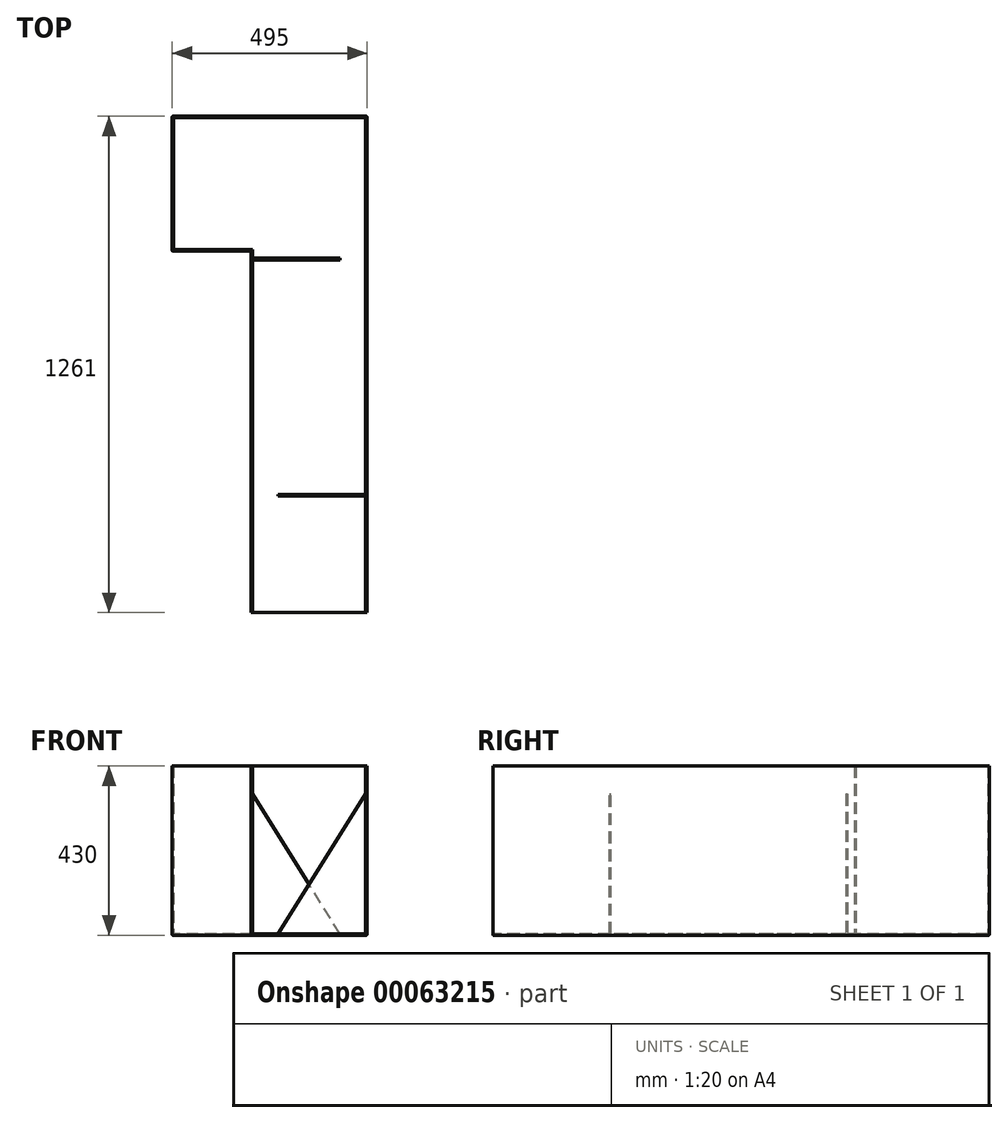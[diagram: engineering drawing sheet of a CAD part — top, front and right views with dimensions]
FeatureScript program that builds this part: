
annotation { "Feature Type Name" : "Feature", "Feature Type Description" : "" }
export const myFeature = defineFeature(function(context is Context, id is Id, definition is map)
    precondition{}
    {
        {
            var Q0;
            Q0=qCreatedBy(makeId("Top.planeOp"),FACE);
            var sketch = newSketch(context, id + "F0", { "sketchPlane" : qUnion([Q0])});
            skLineSegment(sketch, "E0", {"start": v(0, 0) * mm, "end": v(495, 0) * mm});
            skLineSegment(sketch, "E1", {"start": v(200, -343) * mm, "end": v(0, -343) * mm});
            skLineSegment(sketch, "E2", {"start": v(0, -343) * mm, "end": v(0, 0) * mm});
            skLineSegment(sketch, "E3.right", {"start": v(200, -343) * mm, "end": v(200, -1261) * mm});
            skLineSegment(sketch, "E4.left", {"start": v(495, 0) * mm, "end": v(495, -1261) * mm});
            skLineSegment(sketch, "E5.0", {"start": v(491, -4) * mm, "end": v(491, -1261) * mm});
            skLineSegment(sketch, "E5.1", {"start": v(204, -339) * mm, "end": v(204, -1261) * mm});
            skLineSegment(sketch, "E5.2", {"start": v(204, -339) * mm, "end": v(4, -339) * mm});
            skLineSegment(sketch, "E5.3", {"start": v(4, -339) * mm, "end": v(4, -4) * mm});
            skLineSegment(sketch, "E5.4", {"start": v(4, -4) * mm, "end": v(491, -4) * mm});
            skLineSegment(sketch, "E6", {"start": v(204, -1261) * mm, "end": v(200, -1261) * mm});
            skLineSegment(sketch, "E7", {"start": v(491, -1261) * mm, "end": v(495, -1261) * mm});
            skSolve(sketch);
        }
        {
            var Q0;
            Q0=makeQuery(id+"F0.imprint","IMPRINT",FACE,{"disambiguationData":[TD([[makeQuery(id+"F0.imprint","IMPRINT",EDGE,{"derivedFrom":sQuery(id+"F0.wireOp",EDGE,"E0")}),-1.0]])]});
            extrude(context, id + "F1", {"entities" : qUnion([Q0]), "depth" : 426 * mm});
        }
        {
            var Q0;
            Q0=qCreatedBy(makeId("Top.planeOp"),FACE);
            var sketch = newSketch(context, id + "F2", { "sketchPlane" : qUnion([Q0])});
            skLineSegment(sketch, "E8.0", {"start": v(200, -343) * mm, "end": v(0, -343) * mm});
            skLineSegment(sketch, "E9.0", {"start": v(0, -343) * mm, "end": v(0, 0) * mm});
            skLineSegment(sketch, "E10.0", {"start": v(0, 0) * mm, "end": v(0, 0) * mm});
            skLineSegment(sketch, "E11.0", {"start": v(0, 0) * mm, "end": v(495, 0) * mm});
            skLineSegment(sketch, "E12.0", {"start": v(200, -343) * mm, "end": v(200, -343) * mm});
            skLineSegment(sketch, "E13.0", {"start": v(495, 0) * mm, "end": v(495, 0) * mm});
            skLineSegment(sketch, "E14.0", {"start": v(495, 0) * mm, "end": v(495, -1261) * mm});
            skLineSegment(sketch, "E15", {"start": v(495, -1261) * mm, "end": v(200, -1261) * mm});
            skLineSegment(sketch, "E16", {"start": v(200, -1261) * mm, "end": v(200, -343) * mm});
            skSolve(sketch);
        }
        {
            var Q0;
            Q0=qSketchRegion(id+"F2",true);
            extrude(context, id + "F3", {"entities" : qUnion([Q0]), "operationType" : NewBodyOperationType.ADD, "oppositeDirection" : true, "depth" : 4 * mm});
        }
        {
            var Q0;
            Q0=makeQuery(id+"F3.opExtrude","CAP_EDGE",EDGE,{"disambiguationData":[OSD([sQuery(id+"F2.wireOp",EDGE,"E13.0")])],"isStart":false});
            var Q1;
            Q1=makeQuery(id+"F3.opExtrude","CAP_EDGE",EDGE,{"disambiguationData":[OSD([sQuery(id+"F2.wireOp",EDGE,"E8.0")])],"isStart":false});
            var Q2;
            Q2=makeQuery(id+"F3.opExtrude","CAP_EDGE",EDGE,{"disambiguationData":[OSD([sQuery(id+"F2.wireOp",EDGE,"E12.0")])],"isStart":false});
            var Q3;
            Q3=makeQuery(id+"F3.opExtrude","CAP_EDGE",EDGE,{"disambiguationData":[OSD([sQuery(id+"F2.wireOp",EDGE,"E9.0")])],"isStart":false});
            var Q4;
            Q4=makeQuery(id+"F3.opExtrude","CAP_EDGE",EDGE,{"disambiguationData":[OSD([sQuery(id+"F2.wireOp",EDGE,"E11.0")])],"isStart":false});
            var Q5;
            Q5=makeQuery(id+"F3.boolean.opBoolean","MERGE",EDGE,{"derivedFrom":[makeQuery(id+"F1.opExtrude","SWEPT_EDGE",EDGE,{"disambiguationData":[OSD([sQuery(id+"F0.wireOp",EDGE,"E1"),sQuery(id+"F0.wireOp",EDGE,"E3.right")])]}),makeQuery(id+"F3.opExtrude","SWEPT_EDGE",EDGE,{"disambiguationData":[OSD([sQuery(id+"F2.wireOp",EDGE,"E8.0"),sQuery(id+"F2.wireOp",EDGE,"E12.0")])]})]});
            var Q6;
            Q6=makeQuery(id+"F3.boolean.opBoolean","MERGE",EDGE,{"derivedFrom":[makeQuery(id+"F1.opExtrude","SWEPT_EDGE",EDGE,{"disambiguationData":[OSD([sQuery(id+"F0.wireOp",EDGE,"E1"),sQuery(id+"F0.wireOp",EDGE,"E2")])]}),makeQuery(id+"F3.opExtrude","SWEPT_EDGE",EDGE,{"disambiguationData":[OSD([sQuery(id+"F2.wireOp",EDGE,"E8.0"),sQuery(id+"F2.wireOp",EDGE,"E9.0")])]})]});
            var Q7;
            Q7=makeQuery(id+"F3.boolean.opBoolean","MERGE",EDGE,{"derivedFrom":[makeQuery(id+"F1.opExtrude","SWEPT_EDGE",EDGE,{"disambiguationData":[OSD([sQuery(id+"F0.wireOp",EDGE,"E0"),sQuery(id+"F0.wireOp",EDGE,"E2")])]}),makeQuery(id+"F3.opExtrude","SWEPT_EDGE",EDGE,{"disambiguationData":[OSD([sQuery(id+"F2.wireOp",EDGE,"E9.0"),sQuery(id+"F2.wireOp",EDGE,"E11.0")])]})]});
            var Q8;
            Q8=makeQuery(id+"F1.opExtrude","SWEPT_EDGE",EDGE,{"disambiguationData":[OSD([sQuery(id+"F0.wireOp",EDGE,"41269a5a-69f6-4670-b1a7-19bf830e781a"),sQuery(id+"F0.wireOp",EDGE,"E4.right")])]});
            var Q9;
            Q9=makeQuery(id+"F1.opExtrude","SWEPT_EDGE",EDGE,{"disambiguationData":[OSD([sQuery(id+"F0.wireOp",EDGE,"cc5772d9-c29a-4c81-bde5-837d5d9decb7"),sQuery(id+"F0.wireOp",EDGE,"E3.left")])]});
            var Q10;
            Q10=makeQuery(id+"F1.opExtrude","SWEPT_EDGE",EDGE,{"disambiguationData":[OSD([sQuery(id+"F0.wireOp",EDGE,"41269a5a-69f6-4670-b1a7-19bf830e781a"),sQuery(id+"F0.wireOp",EDGE,"05cfef9b-c223-4bdb-b400-77ea615546ad")])]});
            var Q11;
            Q11=makeQuery(id+"F1.opExtrude","SWEPT_EDGE",EDGE,{"disambiguationData":[OSD([sQuery(id+"F0.wireOp",EDGE,"05cfef9b-c223-4bdb-b400-77ea615546ad"),sQuery(id+"F0.wireOp",EDGE,"cc5772d9-c29a-4c81-bde5-837d5d9decb7")])]});
            var Q12;
            Q12=makeQuery(id+"F3.boolean.opBoolean","MERGE",EDGE,{"derivedFrom":[makeQuery(id+"F1.opExtrude","SWEPT_EDGE",EDGE,{"disambiguationData":[OSD([sQuery(id+"F0.wireOp",EDGE,"E0"),sQuery(id+"F0.wireOp",EDGE,"E4.left")])]}),makeQuery(id+"F3.opExtrude","SWEPT_EDGE",EDGE,{"disambiguationData":[OSD([sQuery(id+"F2.wireOp",EDGE,"E11.0"),sQuery(id+"F2.wireOp",EDGE,"E13.0")])]})]});
            var Q13;
            Q13=makeQuery(id+"F3.opExtrude","CAP_EDGE",EDGE,{"disambiguationData":[OSD([sQuery(id+"F2.wireOp",EDGE,"E16")])],"isStart":false});
            var Q14;
            Q14=makeQuery(id+"F3.opExtrude","CAP_EDGE",EDGE,{"disambiguationData":[OSD([sQuery(id+"F2.wireOp",EDGE,"E14.0")])],"isStart":false});
            fillet(context, id + "F4", {"entities" : qUnion([Q0, Q1, Q2, Q3, Q4, Q5, Q6, Q7, Q8, Q9, Q10, Q11, Q12, Q13, Q14]), "radius" : 2 * mm, "tangentPropagation" : true, "allowEdgeOverflow" : false});
        }
        {
            var Q0;
            Q0=makeQuery(id+"F3.boolean.opBoolean","MERGE",FACE,{"derivedFrom":[makeQuery(id+"F1.opExtrude","SWEPT_FACE",FACE,{"disambiguationData":[OSD([sQuery(id+"F0.wireOp",EDGE,"E6")])]}),makeQuery(id+"F1.opExtrude","SWEPT_FACE",FACE,{"disambiguationData":[OSD([sQuery(id+"F0.wireOp",EDGE,"E7")])]}),makeQuery(id+"F3.opExtrude","SWEPT_FACE",FACE,{"disambiguationData":[OSD([sQuery(id+"F2.wireOp",EDGE,"E15")])]})]});
            cPlane(context, id + "F5", {"entities" : qUnion([Q0]), "cplaneType" : CPlaneType.OFFSET, "offset" : 300 * mm, "oppositeDirection" : true, "width" : 150 * mm, "height" : 150 * mm});
        }
        {
            var Q0;
            Q0=qCreatedBy(id+"F5.planeOp",FACE);
            var sketch = newSketch(context, id + "F6", { "sketchPlane" : qUnion([Q0])});
            skLineSegment(sketch, "E17", {"start": v(491, 0) * mm, "end": v(491, 355) * mm});
            skLineSegment(sketch, "E18", {"start": v(491, 355) * mm, "end": v(269, 0) * mm});
            skLineSegment(sketch, "E19", {"start": v(269, 0) * mm, "end": v(491, 0) * mm});
            skSolve(sketch);
        }
        {
            var Q0;
            Q0 = qSketchRegion(id + "F6", true);
            extrude(context, id + "F7", {"entities" : qUnion([Q0]), "operationType" : NewBodyOperationType.ADD, "depth" : 4 * mm});
        }
        {
            var Q0;
            Q0=qCreatedBy(id+"F5.planeOp",FACE);
            cPlane(context, id + "F8", {"entities" : qUnion([Q0]), "cplaneType" : CPlaneType.OFFSET, "offset" : 600 * mm, "oppositeDirection" : true, "width" : 150 * mm, "height" : 150 * mm});
        }
        {
            var Q0;
            Q0=qCreatedBy(id+"F8.planeOp",FACE);
            var sketch = newSketch(context, id + "F9", { "sketchPlane" : qUnion([Q0])});
            skLineSegment(sketch, "E20", {"start": v(204, 0) * mm, "end": v(426, 0) * mm});
            skLineSegment(sketch, "E21", {"start": v(426, 0) * mm, "end": v(204, 355) * mm});
            skLineSegment(sketch, "E22", {"start": v(204, 355) * mm, "end": v(204, 0) * mm});
            skSolve(sketch);
        }
        {
            var Q0;
            Q0 = qSketchRegion(id + "F9", true);
            extrude(context, id + "F10", {"entities" : qUnion([Q0]), "operationType" : NewBodyOperationType.ADD, "depth" : 4 * mm});
        }
    });
